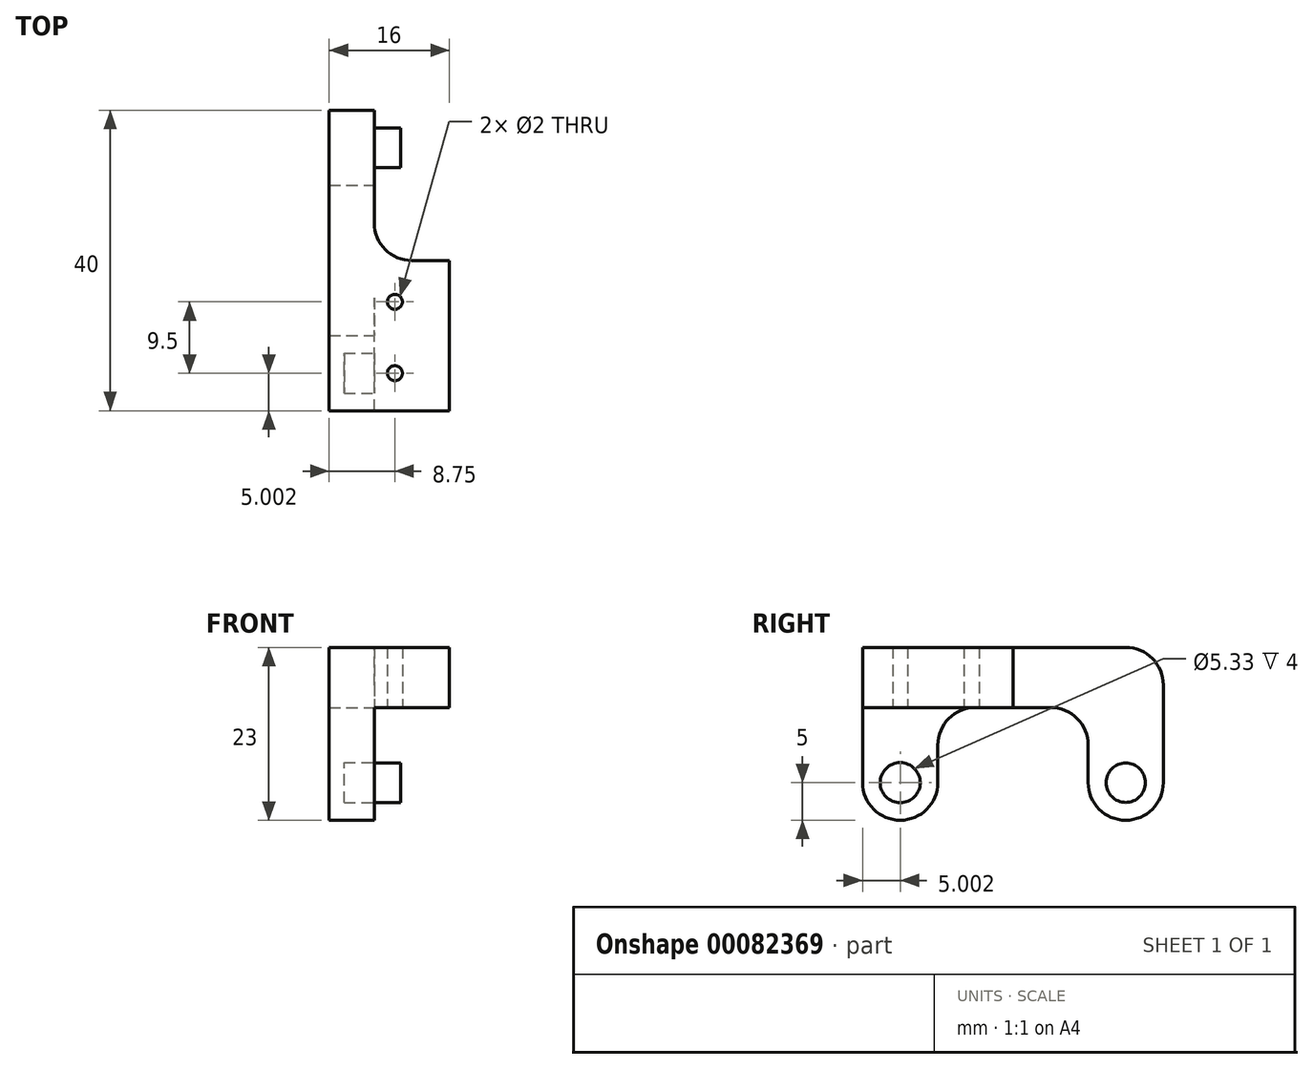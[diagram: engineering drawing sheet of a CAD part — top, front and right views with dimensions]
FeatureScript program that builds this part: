
annotation { "Feature Type Name" : "Feature", "Feature Type Description" : "" }
export const myFeature = defineFeature(function(context is Context, id is Id, definition is map)
    precondition{}
    {
        {
            var Q0;
            Q0=qCreatedBy(makeId("Right.planeOp"),FACE);
            var sketch = newSketch(context, id + "F0", { "sketchPlane" : qUnion([Q0])});
            skCircle(sketch, "E0", {"center": v(22.05, 0) * mm, "radius": 2.62 * mm});
            skCircle(sketch, "E1", {"center": v(-7.95, 0) * mm, "radius": 2.67 * mm});
            skLineSegment(sketch, "E2.bottom", {"start": v(-12.95, 18) * mm, "end": v(7.05, 18) * mm});
            skLineSegment(sketch, "E2.top", {"start": v(-12.95, 10) * mm, "end": v(-2.95, 10) * mm});
            skLineSegment(sketch, "E2.left", {"start": v(-12.95, 18) * mm, "end": v(-12.95, 10) * mm});
            skLineSegment(sketch, "E2.right", {"start": v(27.05, 13) * mm, "end": v(27.05, 10) * mm});
            skLineSegment(sketch, "E3", {"start": v(-2.95, 10) * mm, "end": v(7.05, 10) * mm});
            skLineSegment(sketch, "E4", {"start": v(17.05, 10) * mm, "end": v(27.05, 10) * mm});
            skLineSegment(sketch, "E5", {"start": v(-12.95, 10) * mm, "end": v(-12.95, 0) * mm});
            skLineSegment(sketch, "E6", {"start": v(-7.95, -5) * mm, "end": v(-7.95, -5) * mm});
            skLineSegment(sketch, "E7", {"start": v(-2.95, 0) * mm, "end": v(-2.95, 10) * mm});
            skLineSegment(sketch, "E8", {"start": v(27.05, 10) * mm, "end": v(27.05, 0) * mm});
            skLineSegment(sketch, "E9", {"start": v(22.05, -5) * mm, "end": v(22.05, -5) * mm});
            skLineSegment(sketch, "E10", {"start": v(17.05, 0) * mm, "end": v(17.05, 10) * mm});
            skPoint(sketch, "E11", {"position": v(-7.95, -5) * mm});
            skPoint(sketch, "E12", {"position": v(22.05, -5) * mm});
            skPoint(sketch, "E13.visualSharp", {"position": v(27.05, 18) * mm});
            skArc(sketch, "E13.filletArc", {"start": v(27.05, 13) * mm, "mid": v(25.59, 16.54) * mm, "end": v(22.05, 18) * mm});
            skPoint(sketch, "E14.visualSharp", {"position": v(27.05, -5) * mm});
            skArc(sketch, "E14.filletArc", {"start": v(22.05, -5) * mm, "mid": v(25.59, -3.54) * mm, "end": v(27.05, 0) * mm});
            skPoint(sketch, "E15.visualSharp", {"position": v(17.05, -5) * mm});
            skArc(sketch, "E15.filletArc", {"start": v(17.05, 0) * mm, "mid": v(18.52, -3.54) * mm, "end": v(22.05, -5) * mm});
            skPoint(sketch, "E16.visualSharp", {"position": v(-2.95, -5) * mm});
            skArc(sketch, "E16.filletArc", {"start": v(-7.95, -5) * mm, "mid": v(-4.41, -3.54) * mm, "end": v(-2.95, 0) * mm});
            skPoint(sketch, "E17.visualSharp", {"position": v(-12.95, -5) * mm});
            skArc(sketch, "E17.filletArc", {"start": v(-12.95, 0) * mm, "mid": v(-11.48, -3.54) * mm, "end": v(-7.95, -5) * mm});
            skLineSegment(sketch, "E18", {"start": v(7.05, 18) * mm, "end": v(22.05, 18) * mm});
            skLineSegment(sketch, "E19", {"start": v(7.05, 10) * mm, "end": v(17.05, 10) * mm});
            skLineSegment(sketch, "E20", {"start": v(7.05, 18) * mm, "end": v(7.05, 10) * mm});
            skSolve(sketch);
        }
        {
            var Q0;
            Q0=qCreatedBy(makeId("Top.planeOp"),FACE);
            var sketch = newSketch(context, id + "F1", { "sketchPlane" : qUnion([Q0])});
            skCircle(sketch, "E21", {"center": v(2.75, 1.55) * mm, "radius": 1 * mm});
            skCircle(sketch, "E22", {"center": v(2.75, -7.95) * mm, "radius": 1 * mm});
            skSolve(sketch);
        }
        {
            var Q0;
            Q0 = qSketchRegion(id + "F0", true);
            var Q1;
            Q1=makeQuery(id+"F0.imprint","IMPRINT",FACE,{"disambiguationData":[TD([[makeQuery(id+"F0.imprint","IMPRINT",EDGE,{"derivedFrom":sQuery(id+"F0.wireOp",EDGE,"E1")}),1.0]])]});
            var Q2;
            Q2=makeQuery(id+"F0.imprint","IMPRINT",FACE,{"disambiguationData":[TD([[makeQuery(id+"F0.imprint","IMPRINT",EDGE,{"derivedFrom":sQuery(id+"F0.wireOp",EDGE,"E0")}),1.0]])]});
            extrude(context, id + "F2", {"entities" : qUnion([Q0, Q1, Q2]), "oppositeDirection" : true, "depth" : 6 * mm});
        }
        {
            var Q0;
            Q0=makeQuery(id+"F0.imprint","IMPRINT",FACE,{"disambiguationData":[TD([[makeQuery(id+"F0.imprint","IMPRINT",EDGE,{"derivedFrom":sQuery(id+"F0.wireOp",EDGE,"E0")}),1.0]])]});
            extrude(context, id + "F3", {"entities" : qUnion([Q0]), "operationType" : NewBodyOperationType.ADD, "depth" : 3.5 * mm});
        }
        {
            var Q0;
            Q0=makeQuery(id+"F0.imprint","IMPRINT",FACE,{"disambiguationData":[TD([[makeQuery(id+"F0.imprint","IMPRINT",EDGE,{"derivedFrom":sQuery(id+"F0.wireOp",EDGE,"E1")}),1.0]])]});
            extrude(context, id + "F4", {"entities" : qUnion([Q0]), "operationType" : NewBodyOperationType.REMOVE, "oppositeDirection" : true, "depth" : 4 * mm});
        }
        {
            var Q0;
            Q0=makeQuery(id+"F0.imprint","IMPRINT",FACE,{"disambiguationData":[TD([[makeQuery(id+"F0.imprint","IMPRINT",EDGE,{"derivedFrom":sQuery(id+"F0.wireOp",EDGE,"E2.bottom")}),-1.0]])]});
            extrude(context, id + "F5", {"entities" : qUnion([Q0]), "operationType" : NewBodyOperationType.ADD, "depth" : 10 * mm});
        }
        {
            var Q0;
            Q0=makeQuery(id+"F1.imprint","IMPRINT",FACE,{"disambiguationData":[TD([[makeQuery(id+"F1.imprint","IMPRINT",EDGE,{"derivedFrom":sQuery(id+"F1.wireOp",EDGE,"E21")}),1.0]])]});
            var Q1;
            Q1=makeQuery(id+"F1.imprint","IMPRINT",FACE,{"disambiguationData":[TD([[makeQuery(id+"F1.imprint","IMPRINT",EDGE,{"derivedFrom":sQuery(id+"F1.wireOp",EDGE,"E22")}),1.0]])]});
            extrude(context, id + "F6", {"entities" : qUnion([Q0, Q1]), "operationType" : NewBodyOperationType.REMOVE, "endBound" : BoundingType.THROUGH_ALL, "depth" : 25 * mm});
        }
        {
            var Q0;
            Q0=makeQuery(id+"F5.opExtrude","CAP_EDGE",EDGE,{"disambiguationData":[OSD([sQuery(id+"F0.wireOp",EDGE,"E20")])],"isStart":true});
            var Q1;
            Q1=makeQuery(id+"F2.opExtrude","SWEPT_EDGE",EDGE,{"disambiguationData":[OSD([sQuery(id+"F0.wireOp",EDGE,"E2.top"),sQuery(id+"F0.wireOp",EDGE,"E3"),sQuery(id+"F0.wireOp",EDGE,"E7")])]});
            var Q2;
            Q2=makeQuery(id+"F2.opExtrude","SWEPT_EDGE",EDGE,{"disambiguationData":[OSD([sQuery(id+"F0.wireOp",EDGE,"E4"),sQuery(id+"F0.wireOp",EDGE,"E10"),sQuery(id+"F0.wireOp",EDGE,"E19")])]});
            fillet(context, id + "F7", {"entities" : qUnion([Q0, Q1, Q2]), "radius" : 5 * mm, "tangentPropagation" : true, "allowEdgeOverflow" : false});
        }
    });
